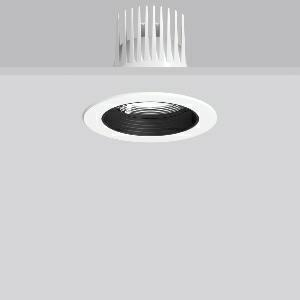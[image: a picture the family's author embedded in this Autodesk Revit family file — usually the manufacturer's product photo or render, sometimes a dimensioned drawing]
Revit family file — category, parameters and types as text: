
# Revit family: heledon_maxi_e_901769_002_0bde
name_source: partatom
category: Lighting Fixtures
units: mm (PartAtom-declared; Revit-internal decimal feet)

## family parameters
Cut with Voids When Loaded = No
Host = Face
Light Source = No
Part Type = Normal
Room Calculation Point = No
Round Connector Dimension = Use Diameter
Shared = No

## types (1)
- HELEDON maxi E (1 x LED Modul 930, 3600 lm, 3000)
    Apparent Load = 35 VA
    Approval mark = CE
    CIE Flux Codes = 96 100 100 100 100
    Color Rendering = 90
    Color Temperature = 3000
    Default Elevation = 1800 mm
    Description = Series: HELEDON maxi
Round recessed downlight. Housing: die-cast aluminium, powder-coated. Black plastic ring and recessed LED to prevent glare from the side. Optical assembly with lens made of plastic (polycarbonate) for the best homogeneous light distribution - can be changed without tools. Best colour rendering index Ra>90. Suitable for Recessed ceiling mounting. Installation without tools thanks to spring fastening system. Including separate LED converter with connecting cable 600 mm.High quality converter without flickering and stroboscopic effect. Through-wiring box (5 pole) available as accessory. The following accessories can be mounted without use of tools: interchangeable lenses, decorative glasses, honeycomb louvre, clear and frosted diffusers, white interchangeable plastic ring. 
Colour: traffic white, matt (RAL 9016)
Diameter: 162 mm
Height: 3 mm
Cut-out diameter: 152 mm
Recess height: 200 mm
Luminaire: recess height: 135 mm
Lamp: LED
Socket: without socket
Colour temperature: 3000K
Colour rendering index (CRI): 92
System power: 35 W
Rated luminous flux: 3600 lm
Luminous efficiency: 103 lm/W
Control gear: Regulated power supply
Protection class: II
Type of protection: IP 20
    Height = 0 mm  [stored 0 ft]
    Lamp = 1 x LED Modul 930
    Lamp Light Flux = 3600 lm
    Lamp count = 1
    Length = 162 mm
    Lifetime = 50000 h
    Luminous efficacy = 103 lm/W
    Manufacturer = RZB
    ModVariant = No
    Model = 901769.002
    Mounting Place = Ceiling
    Mounting Type = Recessed
    Number of Poles = 1
    OnlyDefault = Yes
    Power Factor = 1
    Product Name = HELEDON maxi E
    Product group = Recessed downlights
    ProductGroupID = 402
    Protection Class = Protection class II
    Protection Degree = IP 20
    RLX_Detail_Level = 1
    RLX_Emergency_Light_Flux = 0 lm
    RLX_Emergency_Type = 0
    RLX_Emergency_Type_DB = No
    RlxData = <blob elided: 119645 chars, md5=dbbb9f41>
    Socket = socket
    Standby Power = 0 W
    System Light Flux = 3600 lm
    System Power = 35 W
    Type Comments = Product without accessories
    Type Image = 901663.002.jpg
    URL = http://relux.com
    VarID = ---
    Voltage = 230 V
    Voltage Range = 220-240 V
    Weight = 0.00 kg
    Width = 0 mm  [stored 0 ft]

note: [stored X ft] marks values corroborated as IEEE doubles in the binary element streams (Revit-internal decimal feet)

## geometry (parser evidence)
native form markers: Blend x4, Sweep x12
no freeform markers — native parametric forms only
